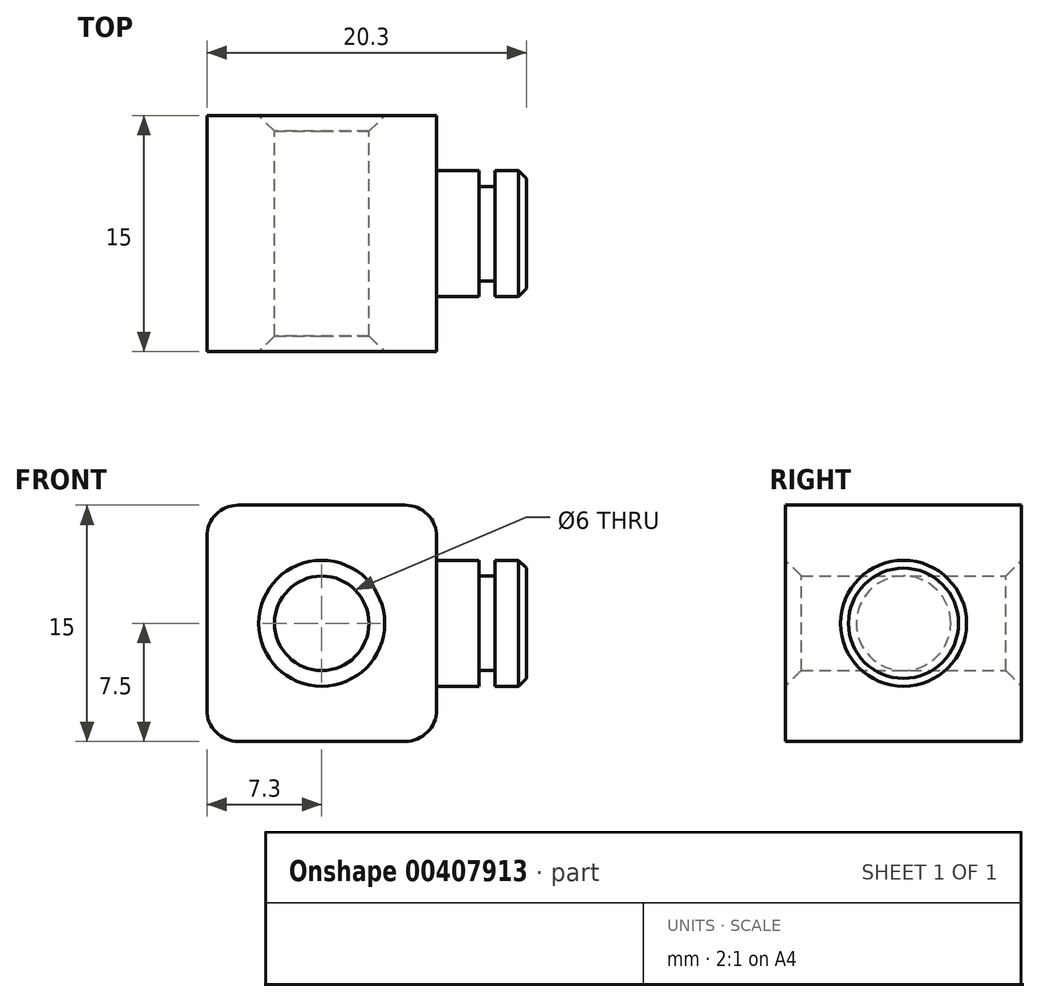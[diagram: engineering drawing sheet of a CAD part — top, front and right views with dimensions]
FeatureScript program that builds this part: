
annotation { "Feature Type Name" : "Feature", "Feature Type Description" : "" }
export const myFeature = defineFeature(function(context is Context, id is Id, definition is map)
    precondition{}
    {
        {
            var Q0;
            Q0=qCreatedBy(makeId("Front.planeOp"),FACE);
            var sketch = newSketch(context, id + "F0", { "sketchPlane" : qUnion([Q0])});
            skLineSegment(sketch, "E0.bottom", {"start": v(7.3, -7.5) * mm, "end": v(-7.3, -7.5) * mm});
            skLineSegment(sketch, "E0.top", {"start": v(7.3, 7.5) * mm, "end": v(-7.3, 7.5) * mm});
            skLineSegment(sketch, "E0.left", {"start": v(7.3, -7.5) * mm, "end": v(7.3, 7.5) * mm});
            skLineSegment(sketch, "E0.right", {"start": v(-7.3, -7.5) * mm, "end": v(-7.3, 7.5) * mm});
            skPoint(sketch, "E0.middle", {"position": v(0, 0) * mm});
            skCircle(sketch, "E1", {"center": v(0, 0) * mm, "radius": 3 * mm});
            skSolve(sketch);
        }
        {
            var Q0;
            Q0=makeQuery(id+"F0.imprint","IMPRINT",FACE,{"disambiguationData":[TD([[makeQuery(id+"F0.imprint","IMPRINT",EDGE,{"derivedFrom":sQuery(id+"F0.wireOp",EDGE,"E0.bottom")}),-1.0]])]});
            extrude(context, id + "F1", {"entities" : qUnion([Q0]), "endBound" : BoundingType.SYMMETRIC, "depth" : 15 * mm});
        }
        {
            var Q0;
            Q0=makeQuery(id+"F1.opExtrude","CAP_EDGE",EDGE,{"disambiguationData":[OSD([sQuery(id+"F0.wireOp",EDGE,"E1")])],"isStart":false});
            var Q1;
            Q1=makeQuery(id+"F1.opExtrude","CAP_EDGE",EDGE,{"disambiguationData":[OSD([sQuery(id+"F0.wireOp",EDGE,"E1")])],"isStart":true});
            chamfer(context, id + "F2", {"entities" : qUnion([Q0, Q1]), "width" : 1 * mm, "tangentPropagation" : true});
        }
        {
            var Q0;
            Q0=makeQuery(id+"F1.opExtrude","SWEPT_FACE",FACE,{"disambiguationData":[OSD([sQuery(id+"F0.wireOp",EDGE,"E0.left")])]});
            var sketch = newSketch(context, id + "F3", { "sketchPlane" : qUnion([Q0])});
            skCircle(sketch, "E2", {"center": v(0, 0) * mm, "radius": 4 * mm});
            skSolve(sketch);
        }
        {
            var Q0;
            Q0=makeQuery(id+"F3.imprint","IMPRINT",FACE,{"disambiguationData":[TD([[makeQuery(id+"F3.imprint","IMPRINT",EDGE,{"derivedFrom":sQuery(id+"F3.wireOp",EDGE,"E2")}),1.0]])]});
            extrude(context, id + "F4", {"entities" : qUnion([Q0]), "operationType" : NewBodyOperationType.ADD, "depth" : ((26 - 14.6) / 2) * mm});
        }
        {
            var Q0;
            Q0=qCreatedBy(makeId("Front.planeOp"),FACE);
            var sketch = newSketch(context, id + "F5", { "sketchPlane" : qUnion([Q0])});
            skLineSegment(sketch, "E3", {"start": v(7.3, 4) * mm, "end": v(13, 4) * mm});
            skLineSegment(sketch, "E4.bottom", {"start": v(11, 4) * mm, "end": v(10, 4) * mm});
            skLineSegment(sketch, "E4.top", {"start": v(11, 3) * mm, "end": v(10, 3) * mm});
            skLineSegment(sketch, "E4.left", {"start": v(11, 4) * mm, "end": v(11, 3) * mm});
            skLineSegment(sketch, "E4.right", {"start": v(10, 4) * mm, "end": v(10, 3) * mm});
            skLineSegment(sketch, "E5", {"start": v(13, 0) * mm, "end": v(8, 0) * mm, "construction": true});
            skLineSegment(sketch, "E6", {"start": v(8.23, 4) * mm, "end": v(13, 4) * mm});
            skLineSegment(sketch, "E7", {"start": v(13, -4) * mm, "end": v(7.3, -4) * mm});
            skLineSegment(sketch, "E8", {"start": v(8.57, 4) * mm, "end": v(13, 4) * mm});
            skSolve(sketch);
        }
        {
            var Q0;
            Q0 = qSketchRegion(id + "F5", true);
            var Q1;
            Q1=sQuery(id+"F5.wireOp",EDGE,"E5");
            revolve(context, id + "F6", {"operationType" : NewBodyOperationType.REMOVE, "entities" : qUnion([Q0]), "axis" : qUnion([Q1]), "revolveType" : RevolveType.FULL, "oppositeDirection" : true});
        }
        {
            var Q0;
            Q0=makeQuery(id+"F4.opExtrude","CAP_EDGE",EDGE,{"disambiguationData":[OSD([sQuery(id+"F3.wireOp",EDGE,"E2")])],"isStart":false});
            chamfer(context, id + "F7", {"entities" : qUnion([Q0]), "width" : .5 * mm, "tangentPropagation" : true});
        }
        {
            var Q0;
            Q0=makeQuery(id+"F1.opExtrude","SWEPT_EDGE",EDGE,{"disambiguationData":[OSD([sQuery(id+"F0.wireOp",EDGE,"E0.top"),sQuery(id+"F0.wireOp",EDGE,"E0.right")])]});
            var Q1;
            Q1=makeQuery(id+"F1.opExtrude","SWEPT_EDGE",EDGE,{"disambiguationData":[OSD([sQuery(id+"F0.wireOp",EDGE,"E0.top"),sQuery(id+"F0.wireOp",EDGE,"E0.left")])]});
            var Q2;
            Q2=makeQuery(id+"F1.opExtrude","SWEPT_EDGE",EDGE,{"disambiguationData":[OSD([sQuery(id+"F0.wireOp",EDGE,"E0.bottom"),sQuery(id+"F0.wireOp",EDGE,"E0.right")])]});
            var Q3;
            Q3=makeQuery(id+"F1.opExtrude","SWEPT_EDGE",EDGE,{"disambiguationData":[OSD([sQuery(id+"F0.wireOp",EDGE,"E0.bottom"),sQuery(id+"F0.wireOp",EDGE,"E0.left")])]});
            fillet(context, id + "F8", {"entities" : qUnion([Q0, Q1, Q2, Q3]), "radius" : 2 * mm, "tangentPropagation" : true, "allowEdgeOverflow" : false});
        }
    });
